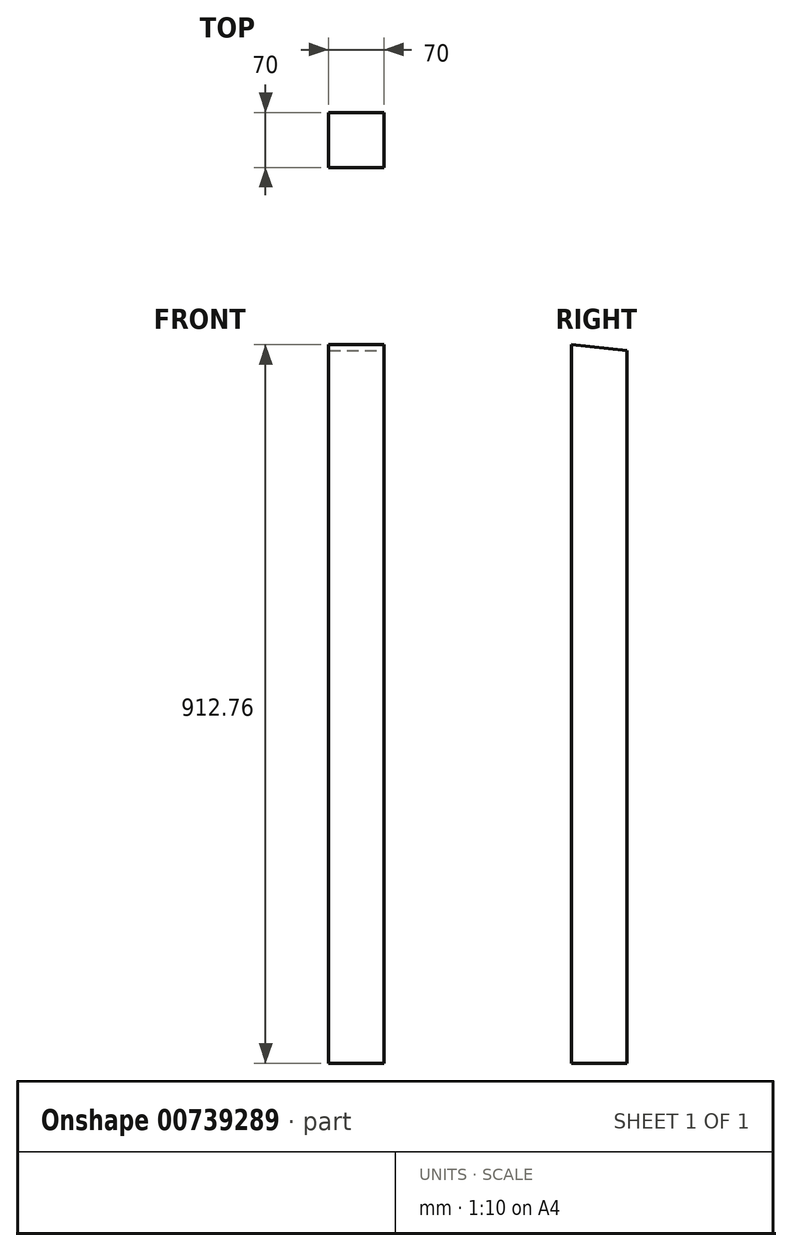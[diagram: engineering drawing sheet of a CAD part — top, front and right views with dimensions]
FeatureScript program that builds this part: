
annotation { "Feature Type Name" : "Feature", "Feature Type Description" : "" }
export const myFeature = defineFeature(function(context is Context, id is Id, definition is map)
    precondition{}
    {
        {
            var Q0;
            Q0=qCreatedBy(makeId("Top.planeOp"),FACE);
            var sketch = newSketch(context, id + "F0", { "sketchPlane" : qUnion([Q0])});
            skLineSegment(sketch, "E0.bottom", {"start": v(-35, 35) * mm, "end": v(35, 35) * mm});
            skLineSegment(sketch, "E0.top", {"start": v(-35, -35) * mm, "end": v(35, -35) * mm});
            skLineSegment(sketch, "E0.left", {"start": v(-35, 35) * mm, "end": v(-35, -35) * mm});
            skLineSegment(sketch, "E0.right", {"start": v(35, 35) * mm, "end": v(35, -35) * mm});
            skSolve(sketch);
        }
        {
            var Q0;
            Q0=makeQuery(id+"F0.imprint","IMPRINT",FACE,{"disambiguationData":[TD([[makeQuery(id+"F0.imprint","IMPRINT",EDGE,{"derivedFrom":sQuery(id+"F0.wireOp",EDGE,"E0.bottom")}),-1.0]])]});
            extrude(context, id + "F1", {"entities" : qUnion([Q0]), "depth" : 1000 * mm, "offsetDistance" : 25 * mm});
        }
        {
            var Q0;
            Q0=makeQuery(id+"F1.opExtrude","SWEPT_FACE",FACE,{"disambiguationData":[OSD([sQuery(id+"F0.wireOp",EDGE,"E0.right")])]});
            var sketch = newSketch(context, id + "F2", { "sketchPlane" : qUnion([Q0])});
            skLineSegment(sketch, "E1", {"start": v(-865, 1000) * mm, "end": v(35, 905.4) * mm});
            skSolve(sketch);
        }
        {
            var Q0;
            {var subQ0=sQuery(id+"F2.wireOp",EDGE,"E1");Q0=makeQuery(id+"F2.imprint","IMPRINT",FACE,{"disambiguationData":[TD([[makeQuery(id+"F2.imprint","IMPRINT",EDGE,{"derivedFrom":subQ0}),1.0]])]});}
            extrude(context, id + "F3", {"entities" : qUnion([Q0]), "operationType" : NewBodyOperationType.REMOVE, "endBound" : BoundingType.UP_TO_NEXT, "oppositeDirection" : true, "depth" : 25 * mm, "offsetDistance" : 25 * mm});
        }
    });
